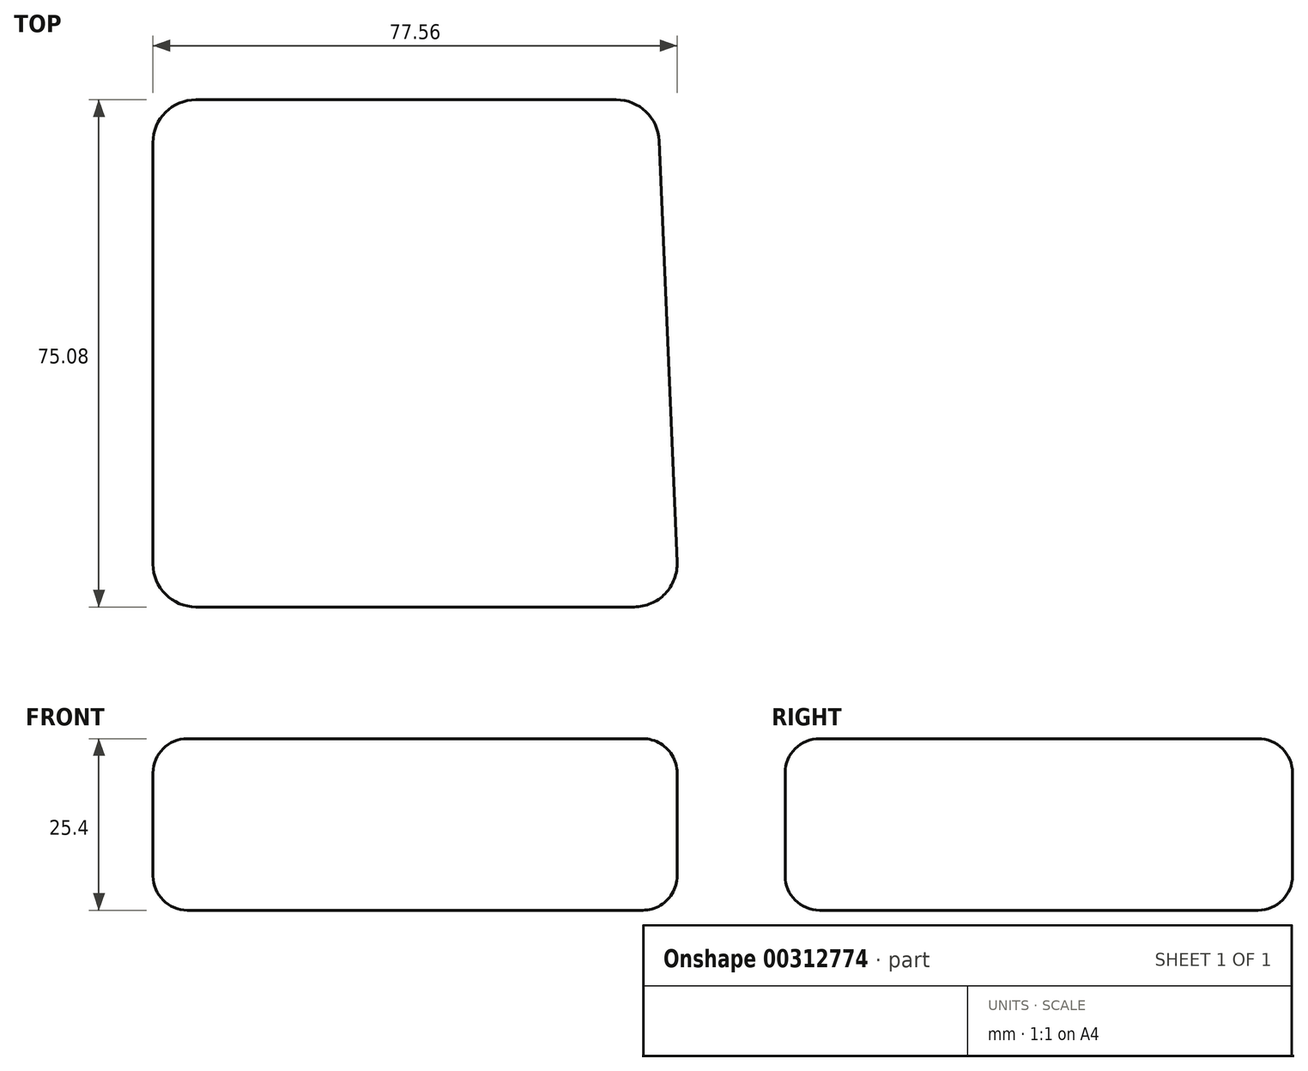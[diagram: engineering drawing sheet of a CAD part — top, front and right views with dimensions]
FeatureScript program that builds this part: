
annotation { "Feature Type Name" : "Feature", "Feature Type Description" : "" }
export const myFeature = defineFeature(function(context is Context, id is Id, definition is map)
    precondition{}
    {
        {
            var Q0;
            Q0=qCreatedBy(makeId("Top.planeOp"),FACE);
            var sketch = newSketch(context, id + "F0", { "sketchPlane" : qUnion([Q0])});
            skLineSegment(sketch, "E0", {"start": v(68.56, 0) * mm, "end": v(6.35, 0) * mm});
            skLineSegment(sketch, "E1", {"start": v(0, -6.35) * mm, "end": v(0, -68.73) * mm});
            skLineSegment(sketch, "E2", {"start": v(6.35, -75.08) * mm, "end": v(71.21, -75.08) * mm});
            skLineSegment(sketch, "E3", {"start": v(77.56, -68.46) * mm, "end": v(74.9, -6.08) * mm});
            skPoint(sketch, "E4.visualSharp", {"position": v(77.84, -75.08) * mm});
            skArc(sketch, "E4.filletArc", {"start": v(71.21, -75.08) * mm, "mid": v(75.8, -73.12) * mm, "end": v(77.56, -68.46) * mm});
            skPoint(sketch, "E5.visualSharp", {"position": v(74.65, 0) * mm});
            skArc(sketch, "E5.filletArc", {"start": v(74.9, -6.08) * mm, "mid": v(72.95, -1.77) * mm, "end": v(68.56, 0) * mm});
            skPoint(sketch, "E6.visualSharp", {"position": v(0, 0) * mm});
            skArc(sketch, "E6.filletArc", {"start": v(6.35, 0) * mm, "mid": v(1.86, -1.86) * mm, "end": v(0, -6.35) * mm});
            skPoint(sketch, "E7.visualSharp", {"position": v(0, -75.08) * mm});
            skArc(sketch, "E7.filletArc", {"start": v(0, -68.73) * mm, "mid": v(1.86, -73.22) * mm, "end": v(6.35, -75.08) * mm});
            skSolve(sketch);
        }
        {
            var Q0;
            Q0=makeQuery(id+"F0.imprint","IMPRINT",FACE,{"disambiguationData":[TD([[makeQuery(id+"F0.imprint","IMPRINT",EDGE,{"derivedFrom":sQuery(id+"F0.wireOp",EDGE,"E0")}),1.0]])]});
            extrude(context, id + "F1", {"entities" : qUnion([Q0]), "depth" : 25.4 * mm});
        }
        {
            var Q0;
            Q0=makeQuery(id+"F1.opExtrude","CAP_EDGE",EDGE,{"disambiguationData":[OSD([sQuery(id+"F0.wireOp",EDGE,"E2")])],"isStart":false});
            fillet(context, id + "F2", {"entities" : qUnion([Q0]), "radius" : 5.08 * mm, "tangentPropagation" : true, "allowEdgeOverflow" : false});
        }
        {
            var Q0;
            Q0=makeQuery(id+"F1.opExtrude","CAP_EDGE",EDGE,{"disambiguationData":[OSD([sQuery(id+"F0.wireOp",EDGE,"E2")])],"isStart":true});
            var Q1;
            Q1=makeQuery(id+"F1.opExtrude","CAP_EDGE",EDGE,{"disambiguationData":[OSD([sQuery(id+"F0.wireOp",EDGE,"E3")])],"isStart":true});
            fillet(context, id + "F3", {"entities" : qUnion([Q0, Q1]), "radius" : 5.08 * mm, "tangentPropagation" : true, "allowEdgeOverflow" : false});
        }
    });
